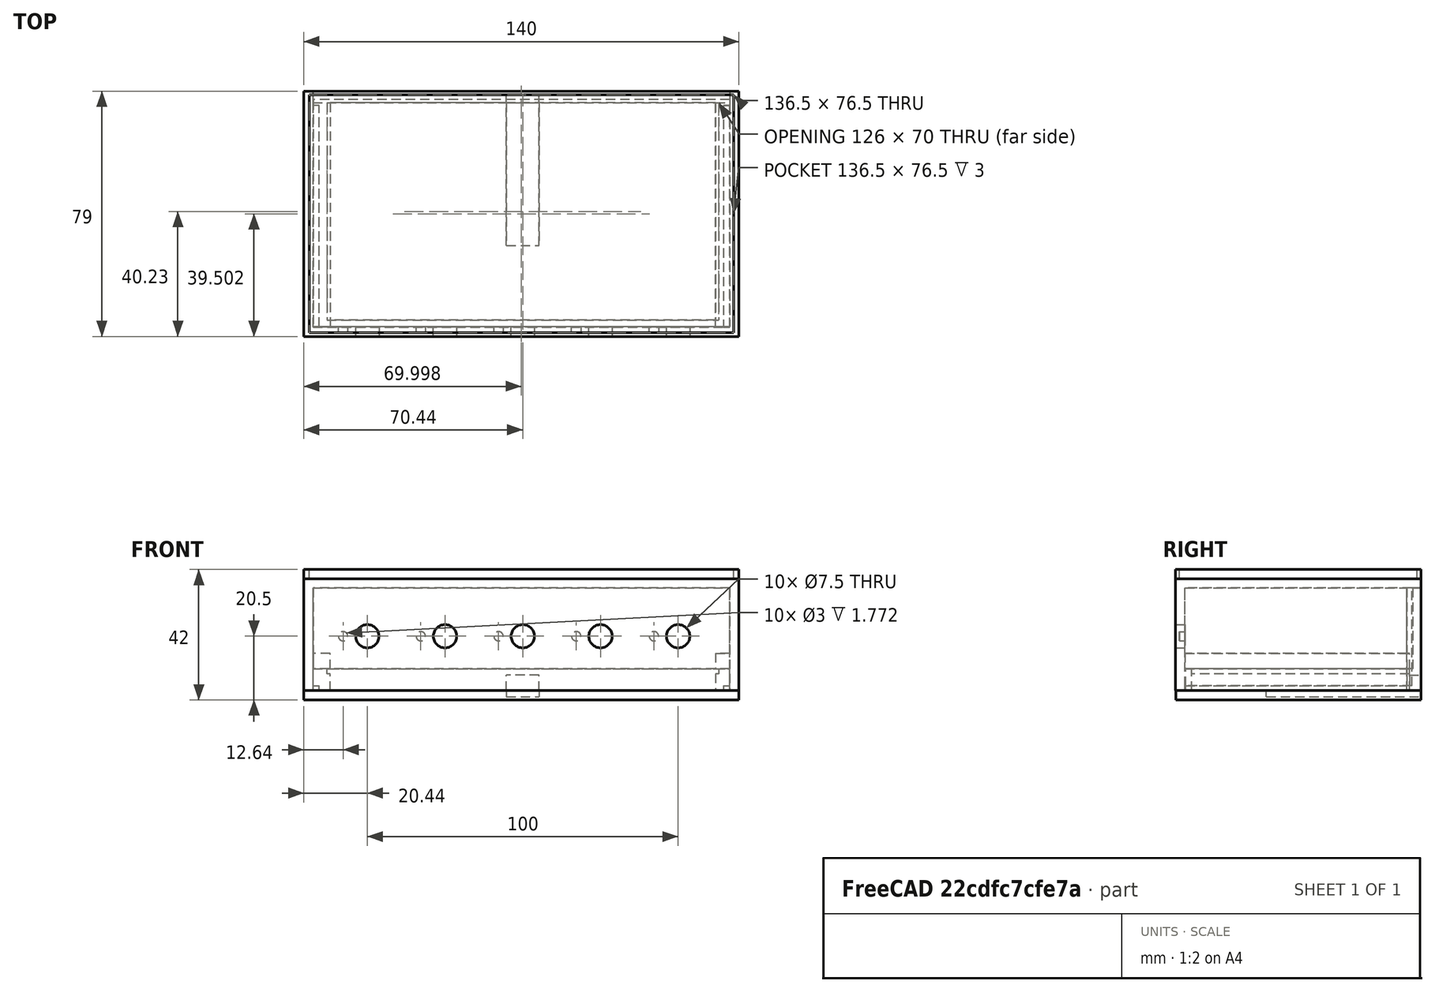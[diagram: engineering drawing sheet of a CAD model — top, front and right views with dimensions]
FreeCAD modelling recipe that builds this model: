
FCSTD DOCUMENT  (FreeCAD 0.18R4 (GitTag))
Label: Case_Top
License: All rights reserved
LicenseURL: http://en.wikipedia.org/wiki/All_rights_reserved
objects: Part::Extrusion×8, Part::Cut×6, Sketcher::SketchObject×6, Part::Feature×5, Part::Part2DObjectPython×3, Part::FeaturePython×3, Mesh::Feature×2, Part::Box×1
note: 32 computed .brp shape members not serialized (recipe doc carries the construction recipe); baked Part::Feature solids carry a one-line shape summary decoded from their .brp

FEATURE [Part::Feature] Cut002001  label="Top-Combine"
  shape: bbox 140 x 79 x 39 mm, 30 faces (baked)
FEATURE [Part::Part2DObjectPython] Rectangle  # Draft 2D object (typed FeaturePython)
  ChamferSize = 0
  Columns = 1
  FilletRadius = 0
  Height = 75.7944
  Length = 134.001
  MakeFace = false
  Placement = pos=(-67.4431,-19.022,0) rot=(0,0,1;0rad)
  Rows = 1
FEATURE [Part::Extrusion] Extrude
  Base = -> Rectangle
  Dir = (0,0,1)
  DirMode = 2
  FaceMakerClass = Part::FaceMakerBullseye
  LengthFwd = 33
  LengthRev = 0
  Placement = pos=(0,0,-1.5) rot=(0,0,1;0rad)
  Solid = true
  Symmetric = true
FEATURE [Part::Part2DObjectPython] Rectangle002  # Draft 2D object (typed FeaturePython)
  ChamferSize = 0
  Columns = 1
  FilletRadius = 0
  Height = 78.9686
  Length = 140
  MakeFace = false
  Placement = pos=(-70.4431,-22.1962,-18) rot=(0,0,1;0rad)
  Rows = 1
FEATURE [Part::Extrusion] Extrude018
  Base = -> Rectangle002
  Dir = (0,0,1)
  DirMode = 2
  FaceMakerClass = Part::FaceMakerBullseye
  LengthFwd = 3
  LengthRev = 0
  Reversed = true
  Solid = true
  Symmetric = false
FEATURE [Part::FeaturePython] Embed  # WARN: FeaturePython — macro-defined, semantics opaque (R4)
  Base = -> Extrude
  Tolerance = 0
  Tool = -> Extrude018
FEATURE [Part::FeaturePython] Cutout  # WARN: FeaturePython — macro-defined, semantics opaque (R4)
  Base = -> Embed
  Tolerance = 0
  Tool = -> Cut002001
FEATURE [Part::Feature] Cut002002  label="Top-whole"
  Placement = pos=(0,-17,0) rot=(0,0,1;0rad)
  shape: bbox 140 x 79 x 39 mm, 30 faces (baked)
FEATURE [Part::Part2DObjectPython] Rectangle003  # Draft 2D object (typed FeaturePython)
  ChamferSize = 0
  Columns = 1
  FilletRadius = 0
  Height = 74
  Length = 135
  MakeFace = false
  Placement = pos=(-68,-20,15) rot=(0,0,1;0rad)
  Rows = 1
FEATURE [Part::Extrusion] Extrude019
  Base = -> Rectangle003
  Dir = (0,0,1)
  DirMode = 2
  FaceMakerClass = Part::FaceMakerBullseye
  LengthFwd = 26
  LengthRev = 0
  Reversed = true
  Solid = true
  Symmetric = false
FEATURE [Part::Cut] Cut
  Base = -> Cutout
  Placement = pos=(0,-17,0) rot=(0,0,1;0rad)
  Tool = -> Extrude019
FEATURE [Sketcher::SketchObject] Sketch
  Placement = pos=(0,0,0) rot=(1,0,0;1.5708rad)
  sketch-geometry (4):
    g0: LineSegment StartX=-62 StartY=-11 StartZ=0 EndX=62 EndY=-11 EndZ=0
    g1: LineSegment StartX=62 StartY=-11 StartZ=0 EndX=62 EndY=-18 EndZ=0
    g2: LineSegment StartX=62 StartY=-18 StartZ=0 EndX=-62 EndY=-18 EndZ=0
    g3: LineSegment StartX=-62 StartY=-18 StartZ=0 EndX=-62 EndY=-11 EndZ=0
  constraints (12):
    c: Coincident(g0,g1)
    c: Coincident(g1,g2)
    c: Coincident(g2,g3)
    c: Coincident(g3,g0)
    c: Horizontal(g0)
    c: Horizontal(g2)
    c: Vertical(g1)
    c: Vertical(g3)
    c: DistanceX(g2,g1) = 124
    c: DistanceY(g2,g0) = 7
    c: DistanceX(g0,g-1) = 62
    c: DistanceY(g0,g-1) = 11
FEATURE [Part::Extrusion] Extrude020
  Base = -> Sketch
  Dir = (0,-1,0)
  DirMode = 2
  FaceMakerClass = Part::FaceMakerBullseye
  LengthFwd = 70
  LengthRev = 0
  Placement = pos=(0,1,0) rot=(0,0,1;0rad)
  Solid = true
  Symmetric = true
FEATURE [Part::Cut] Cut002003
  Base = -> Cut
  Tool = -> Extrude020
FEATURE [Sketcher::SketchObject] Sketch001
  Placement = pos=(0,0,0) rot=(1,0,0;1.5708rad)
  sketch-geometry (4):
    g0: LineSegment StartX=-63 StartY=-11 StartZ=0 EndX=63 EndY=-11 EndZ=0
    g1: LineSegment StartX=63 StartY=-11 StartZ=0 EndX=63 EndY=-12.6 EndZ=0
    g2: LineSegment StartX=63 StartY=-12.6 StartZ=0 EndX=-63 EndY=-12.6 EndZ=0
    g3: LineSegment StartX=-63 StartY=-12.6 StartZ=0 EndX=-63 EndY=-11 EndZ=0
  constraints (12):
    c: Coincident(g0,g1)
    c: Coincident(g1,g2)
    c: Coincident(g2,g3)
    c: Coincident(g3,g0)
    c: Horizontal(g0)
    c: Horizontal(g2)
    c: Vertical(g1)
    c: Vertical(g3)
    c: DistanceX(g2,g1) = 126
    c: DistanceY(g2,g0) = 1.6
    c: DistanceX(g0,g-1) = 63
    c: DistanceY(g0,g-1) = 11
FEATURE [Part::Extrusion] Extrude021
  Base = -> Sketch001
  Dir = (0,-1,2e-16)
  DirMode = 2
  FaceMakerClass = Part::FaceMakerBullseye
  LengthFwd = 70
  LengthRev = 0
  Placement = pos=(0,1,0) rot=(0,0,1;0rad)
  Solid = true
  Symmetric = true
FEATURE [Part::Cut] Cut002004
  Base = -> Cut002003
  Tool = -> Extrude021
FEATURE [Part::Box] Box  label="Cube"
  AttacherType = Attacher::AttachEngine3D
  Height = 7
  Length = 10.5
  Placement = pos=(-5.25,-10,-20) rot=(0,0,1;0rad)
  Width = 50
FEATURE [Part::Feature] Cut002005001  label="Bottom"
  shape: bbox 140 x 78.97 x 36 mm, 42 faces (baked)
FEATURE [Sketcher::SketchObject] Sketch002  label="Pots - Origin"
  Placement = pos=(0,0,0) rot=(1,0,0;1.5708rad)
  sketch-geometry (16):
    g0: Circle CenterX=0 CenterY=-0.5 CenterZ=0 NormalX=0 NormalY=0 NormalZ=1 AngleXU=0 Radius=3.75
    g1: Circle CenterX=-7.8 CenterY=-0.5 CenterZ=0 NormalX=0 NormalY=0 NormalZ=1 AngleXU=0 Radius=1.5
    g2: GeomPoint X=62.5 Y=0 Z=0
    g3: GeomPoint X=37.5 Y=0 Z=0
    g4: GeomPoint X=12.5 Y=0 Z=0
    g5: GeomPoint X=-12.5 Y=0 Z=0
    g6: GeomPoint X=-37.5 Y=0 Z=0
    g7: GeomPoint X=-62.5 Y=0 Z=0
    g8: Circle CenterX=17.2 CenterY=-0.5 CenterZ=0 NormalX=0 NormalY=0 NormalZ=1 AngleXU=0 Radius=1.5
    g9: Circle CenterX=25 CenterY=-0.5 CenterZ=0 NormalX=0 NormalY=0 NormalZ=1 AngleXU=0 Radius=3.75
    g10: Circle CenterX=42.2 CenterY=-0.5 CenterZ=0 NormalX=0 NormalY=0 NormalZ=1 AngleXU=0 Radius=1.5
    g11: Circle CenterX=50 CenterY=-0.5 CenterZ=0 NormalX=0 NormalY=0 NormalZ=1 AngleXU=0 Radius=3.75
    g12: Circle CenterX=-32.8 CenterY=-0.5 CenterZ=0 NormalX=0 NormalY=0 NormalZ=1 AngleXU=0 Radius=1.5
    g13: Circle CenterX=-25 CenterY=-0.5 CenterZ=0 NormalX=0 NormalY=0 NormalZ=1 AngleXU=0 Radius=3.75
    g14: Circle CenterX=-57.8 CenterY=-0.5 CenterZ=0 NormalX=0 NormalY=0 NormalZ=1 AngleXU=0 Radius=1.5
    g15: Circle CenterX=-50 CenterY=-0.5 CenterZ=0 NormalX=0 NormalY=0 NormalZ=1 AngleXU=0 Radius=3.75
  constraints (42):
    c: Diameter(g0) = 7.5
    c: Diameter(g1) = 3
    c: Horizontal(g1,g0)
    c: DistanceX(g1,g0) = 7.8
    c: DistanceX(g0,g-1) = 0
    c: DistanceY(g2,g-1) = 0
    c: DistanceX(g3,g2) = 25
    c: DistanceX(g4,g3) = 25
    c: DistanceX(g5,g4) = 25
    c: DistanceX(g6,g5) = 25
    c: DistanceX(g7,g6) = 25
    c: Horizontal(g7,g6)
    c: Horizontal(g6,g5)
    c: Horizontal(g5,g4)
    c: Horizontal(g4,g3)
    c: Horizontal(g3,g2)
    c: DistanceX(g9,g3) = 12.5
    c: DistanceX(g8,g9) = 7.8
    c: Diameter(g9) = 7.5
    c: Diameter(g8) = 3
    c: Diameter(g10) = 3
    c: Diameter(g11) = 7.5
    c: DistanceX(g11,g2) = 12.5
    c: DistanceX(g10,g11) = 7.8
    c: Diameter(g13) = 7.5
    c: Diameter(g12) = 3
    c: Diameter(g15) = 7.5
    c: Diameter(g14) = 3
    c: DistanceX(g13,g5) = 12.5
    c: DistanceX(g12,g13) = 7.8
    c: DistanceX(g15,g6) = 12.5
    c: DistanceX(g14,g15) = 7.8
    c: Horizontal(g1,g13)
    c: Horizontal(g13,g12)
    c: Horizontal(g12,g15)
    c: Horizontal(g15,g14)
    c: Horizontal(g0,g8)
    c: Horizontal(g8,g9)
    c: Horizontal(g9,g10)
    c: Horizontal(g10,g11)
    c: DistanceY(g0,g-1) = 0.5
    c: DistanceX(g0,g4) = 12.5
FEATURE [Sketcher::SketchObject] Sketch003  label="Pots - Small Holes"
  Placement = pos=(0,0,0) rot=(1,0,0;1.5708rad)
  sketch-geometry (11):
    g0: Circle CenterX=-7.8 CenterY=-0.5 CenterZ=0 NormalX=0 NormalY=0 NormalZ=1 AngleXU=0 Radius=1.5
    g1: GeomPoint X=62.5 Y=0 Z=0
    g2: GeomPoint X=37.5 Y=0 Z=0
    g3: GeomPoint X=12.5 Y=0 Z=0
    g4: GeomPoint X=-12.5 Y=0 Z=0
    g5: GeomPoint X=-37.5 Y=0 Z=0
    g6: GeomPoint X=-62.5 Y=0 Z=0
    g7: Circle CenterX=17.2 CenterY=-0.5 CenterZ=0 NormalX=0 NormalY=0 NormalZ=1 AngleXU=0 Radius=1.5
    g8: Circle CenterX=42.2 CenterY=-0.5 CenterZ=0 NormalX=0 NormalY=0 NormalZ=1 AngleXU=0 Radius=1.5
    g9: Circle CenterX=-32.8 CenterY=-0.5 CenterZ=0 NormalX=0 NormalY=0 NormalZ=1 AngleXU=0 Radius=1.5
    g10: Circle CenterX=-57.8 CenterY=-0.5 CenterZ=0 NormalX=0 NormalY=0 NormalZ=1 AngleXU=0 Radius=1.5
  constraints (26):
    c: Diameter(g0) = 3
    c: DistanceY(g1,g-1) = 0
    c: DistanceX(g2,g1) = 25
    c: DistanceX(g3,g2) = 25
    c: DistanceX(g4,g3) = 25
    c: DistanceX(g5,g4) = 25
    c: DistanceX(g6,g5) = 25
    c: Diameter(g7) = 3
    c: Diameter(g8) = 3
    c: Diameter(g9) = 3
    c: Diameter(g10) = 3
    c: DistanceX(g8,g1) = 20.3
    c: DistanceX(g7,g2) = 20.3
    c: DistanceX(g0,g3) = 20.3
    c: DistanceX(g9,g4) = 20.3
    c: DistanceX(g10,g5) = 20.3
    c: DistanceY(g0,g-1) = 0.5
    c: Horizontal(g0,g7)
    c: Horizontal(g7,g8)
    c: Horizontal(g8,g9)
    c: Horizontal(g9,g10)
    c: Horizontal(g-1,g4)
    c: Horizontal(g4,g3)
    c: Horizontal(g3,g5)
    c: Horizontal(g5,g2)
    c: Horizontal(g2,g6)
FEATURE [Sketcher::SketchObject] Sketch004  label="Pots - Shaft"
  Placement = pos=(0,0,0) rot=(1,0,0;1.5708rad)
  sketch-geometry (11):
    g0: Circle CenterX=0 CenterY=-0.5 CenterZ=0 NormalX=0 NormalY=0 NormalZ=1 AngleXU=0 Radius=3.75
    g1: GeomPoint X=62.5 Y=0 Z=0
    g2: GeomPoint X=37.5 Y=0 Z=0
    g3: GeomPoint X=12.5 Y=0 Z=0
    g4: GeomPoint X=-12.5 Y=0 Z=0
    g5: GeomPoint X=-37.5 Y=0 Z=0
    g6: GeomPoint X=-62.5 Y=0 Z=0
    g7: Circle CenterX=25 CenterY=-0.5 CenterZ=0 NormalX=0 NormalY=0 NormalZ=1 AngleXU=0 Radius=3.75
    g8: Circle CenterX=50 CenterY=-0.5 CenterZ=0 NormalX=0 NormalY=0 NormalZ=1 AngleXU=0 Radius=3.75
    g9: Circle CenterX=-25 CenterY=-0.5 CenterZ=0 NormalX=0 NormalY=0 NormalZ=1 AngleXU=0 Radius=3.75
    g10: Circle CenterX=-50 CenterY=-0.5 CenterZ=0 NormalX=0 NormalY=0 NormalZ=1 AngleXU=0 Radius=3.75
  constraints (27):
    c: Diameter(g0) = 7.5
    c: DistanceX(g0,g-1) = 0
    c: DistanceY(g1,g-1) = 0
    c: DistanceX(g2,g1) = 25
    c: DistanceX(g3,g2) = 25
    c: DistanceX(g4,g3) = 25
    c: DistanceX(g5,g4) = 25
    c: DistanceX(g6,g5) = 25
    c: Horizontal(g6,g5)
    c: Horizontal(g5,g4)
    c: Horizontal(g4,g3)
    c: Horizontal(g3,g2)
    c: Horizontal(g2,g1)
    c: DistanceX(g7,g2) = 12.5
    c: Diameter(g7) = 7.5
    c: Diameter(g8) = 7.5
    c: DistanceX(g8,g1) = 12.5
    c: Diameter(g9) = 7.5
    c: Diameter(g10) = 7.5
    c: DistanceX(g9,g4) = 12.5
    c: DistanceX(g10,g5) = 12.5
    c: DistanceY(g0,g-1) = 0.5
    c: DistanceX(g0,g3) = 12.5
    c: Horizontal(g0,g9)
    c: Horizontal(g9,g7)
    c: Horizontal(g7,g10)
    c: Horizontal(g10,g8)
FEATURE [Part::Extrusion] Extrude022
  Base = -> Sketch004
  Dir = (0,-1,2e-16)
  DirMode = 2
  FaceMakerClass = Part::FaceMakerBullseye
  LengthFwd = 40
  LengthRev = 0
  Solid = true
  Symmetric = false
FEATURE [Part::Extrusion] Extrude023
  Base = -> Sketch003
  Dir = (0,-1,2e-16)
  DirMode = 2
  FaceMakerClass = Part::FaceMakerBullseye
  LengthFwd = 38
  LengthRev = 0
  Solid = true
  Symmetric = false
FEATURE [Part::Cut] Cut002005002
  Base = -> Cut002002
  Tool = -> Extrude023
FEATURE [Part::Cut] Cut002005003
  Base = -> Cut002005002
  Tool = -> Extrude022
FEATURE [Part::Cut] Cut002005
  Base = -> Cut002004
  Tool = -> Box
FEATURE [Part::Feature] Cut002005003001  label="Top02"
  shape: bbox 140 x 79 x 39 mm, 45 faces (baked)
FEATURE [Sketcher::SketchObject] Sketch005
  AttachmentOffset = pos=(0,0,-11) rot=(0,0,1;0rad)
  MapMode = 2
  Placement = pos=(0,0,-11) rot=(0,0,1;0rad)
  Support = -> [Cut002005]
  sketch-geometry (8):
    g0: LineSegment StartX=-68 StartY=36 StartZ=0 EndX=-62 EndY=36 EndZ=0
    g1: LineSegment StartX=-62 StartY=36 StartZ=0 EndX=-62 EndY=-37 EndZ=0
    g2: LineSegment StartX=-62 StartY=-37 StartZ=0 EndX=-68 EndY=-37 EndZ=0
    g3: LineSegment StartX=-68 StartY=-37 StartZ=0 EndX=-68 EndY=36 EndZ=0
    g4: LineSegment StartX=68 StartY=-37 StartZ=0 EndX=62 EndY=-37 EndZ=0
    g5: LineSegment StartX=62 StartY=-37 StartZ=0 EndX=62 EndY=36 EndZ=0
    g6: LineSegment StartX=62 StartY=36 StartZ=0 EndX=68 EndY=36 EndZ=0
    g7: LineSegment StartX=68 StartY=36 StartZ=0 EndX=68 EndY=-37 EndZ=0
  constraints (24):
    c: Coincident(g0,g1)
    c: Coincident(g1,g2)
    c: Coincident(g2,g3)
    c: Coincident(g3,g0)
    c: Horizontal(g0)
    c: Horizontal(g2)
    c: Vertical(g1)
    c: Vertical(g3)
    c: DistanceX(g0,g-1) = 68
    c: DistanceX(g0,g0) = 6
    c: DistanceY(g2,g0) = 73
    c: DistanceY(g1,g-1) = 37
    c: Coincident(g4,g5)
    c: Coincident(g5,g6)
    c: Coincident(g6,g7)
    c: Coincident(g7,g4)
    c: Horizontal(g4)
    c: Horizontal(g6)
    c: Vertical(g5)
    c: Vertical(g7)
    c: DistanceX(g-1,g6) = 68
    c: DistanceX(g5,g6) = 6
    c: DistanceY(g4,g6) = 73
    c: DistanceY(g4,g-1) = 37
FEATURE [Part::Extrusion] Extrude024
  Base = -> Sketch005
  Dir = (0,0,1)
  DirMode = 2
  FaceMakerClass = Part::FaceMakerBullseye
  LengthFwd = 5
  LengthRev = 0
  Solid = true
  Symmetric = false
FEATURE [Part::FeaturePython] Embed001  # WARN: FeaturePython — macro-defined, semantics opaque (R4)
  Base = -> Cut002005003001
  Tolerance = 0
  Tool = -> Extrude024
FEATURE [Part::Feature] Embed001001  label="Top"
  shape: bbox 140 x 79 x 39 mm, 55 faces (baked)
FEATURE [Mesh::Feature] Mesh  label="Bottom (Meshed)"
FEATURE [Mesh::Feature] Mesh001  label="Top (Meshed)"
